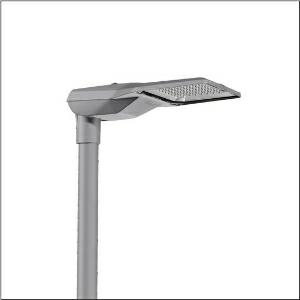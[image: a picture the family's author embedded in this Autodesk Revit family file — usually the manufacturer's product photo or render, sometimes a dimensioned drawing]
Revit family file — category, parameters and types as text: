
# Revit family: streetlight_sl_21_midi___st1_0ab_5xe3m33s08nb_0fd6
name_source: partatom
category: Lighting Fixtures
units: mm (PartAtom-declared; Revit-internal decimal feet)

## family parameters
Cut with Voids When Loaded = No
Host = Face
Light Source = No
Part Type = Normal
Room Calculation Point = No
Round Connector Dimension = Use Diameter
Shared = No

## types (1)
- --- (1 x LED, 19980 lm, 151.2 W, 3000K)
    Apparent Load = 151 VA
    CIE Flux Codes = 40 74 97 100 100
    Color Rendering = 70
    Color Temperature = 3000K
    Default Elevation = 1800 mm
    Description = Streetlight SL 21 midi, mast luminaire, primary light control with lens, of PMMA, primary optical cover: cover, of toughened safety glass, transparent, light distribution: ST1.0aB, light emission: direct distribution, primary light characteristic: asymmetric, installation type: side-entry, post-top, LED, High Power LED, rated luminous flux: 19.980lm, luminous efficacy: 132lm/W, light colour: 730, colour temperature: 3000K, control gear: D4i, control: flexible luminous flux parameterisation, time-dependent luminous flux control, constant luminous flux control, overheat protection, pre-setting: logarithmic dimming characteristic, mains connection: 230..240V, AC, 50/60Hz, start of lifetime: 151W, end of service life: 157W, reduction: 70W, luminaire housing, of diecast aluminium, powder-coated, Siteco® metallic grey (DB 702S), corrosivity category C5 mid according to DIN EN ISO 12944, please order mast flange separately, inclination adjustable: 0°, 5°, 10°, 15°, sealing non-destructively replaceable, multi-level sealing system, length: 644mm, width: 335mm, height: 110mm, mast flange for spigot size: 42mm (side-entry): 5XC10008XM4, 60/48mm (side-entry/post-top): 5XC10108XM2, 76/60mm (side-entry/post-top): 5XC10108XM1, mounting height: 4..8m, Smart Interface above, protection rating (complete): IP66, insulation class (complete): insulation class II (safety insulation), certification: CE, ENEC, ENEC+, VDE, impact resistance: IK10, permissible operating ambient temperature for outdoor applications: -40..+50°C, standard-compliant lighting for roads and squares, packaging unit: 1 piece

Light Distribution: ST1.0aB
    Height = 111 mm
    Lamp = 1 x LED
    Lamp Light Flux = 19980 lm
    Lamp Power = 151.2 W
    Lamp count = 1
    Length = 644 mm
    Luminous efficacy = 132 lm/W
    Manufacturer = Siteco
    ModVariant = No
    Model = 5XE3M33S08NB
    Number of Poles = 1
    OnlyDefault = Yes
    Power Factor = 1
    Product Name = Streetlight SL 21 midi | ST1.0aB
    Product group = mast luminaire | pylon top
    ProductGroupID = 6100
    Protection Class = Protection class II
    Protection Degree = IP 66
    RLX_Detail_Level = 1
    RLX_Emergency_Light_Flux = 0 lm
    RLX_Emergency_Type = 0
    RLX_Emergency_Type_DB = No
    RlxData = <blob elided: 26921 chars, md5=ccf2e72e>
    Socket = socket
    Standby Power = 0 W
    System Light Flux = 19980 lm
    System Power = 151 W
    Type Comments = factory setting: luminous flux: 100 % | dim-lin: 254 | 802 mA
    Type Image = l_1004302.jpg
    URL = http://relux.com
    VarID = @adj_189611
    Voltage = 0 V
    Weight = 0.00 kg
    Width = 336 mm

## geometry (parser evidence)
native form markers: Blend x4, Sweep x10
no freeform markers — native parametric forms only
